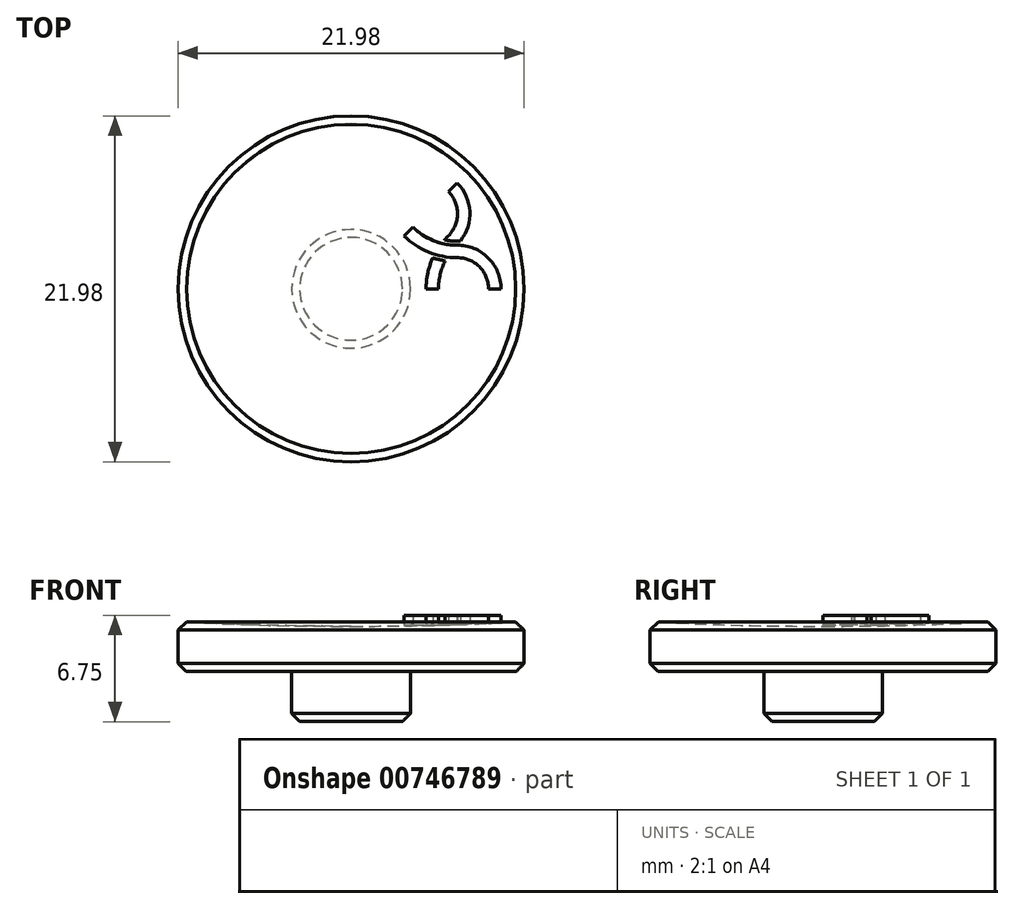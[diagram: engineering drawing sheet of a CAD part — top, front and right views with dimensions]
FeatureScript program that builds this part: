
annotation { "Feature Type Name" : "Feature", "Feature Type Description" : "" }
export const myFeature = defineFeature(function(context is Context, id is Id, definition is map)
    precondition{}
    {
        {
            var Q0;
            Q0=qCreatedBy(makeId("Top.planeOp"),FACE);
            var sketch = newSketch(context, id + "F0", { "sketchPlane" : qUnion([Q0])});
            skCircle(sketch, "E0", {"center": v(0, 0) * mm, "radius": 10.99 * mm});
            skCircle(sketch, "E1", {"center": v(0, 0) * mm, "radius": 3.77 * mm});
            skSolve(sketch);
        }
        {
            var Q0;
            Q0=makeQuery(id+"F0.imprint","IMPRINT",FACE,{"disambiguationData":[TD([[makeQuery(id+"F0.imprint","IMPRINT",EDGE,{"derivedFrom":sQuery(id+"F0.wireOp",EDGE,"E1")}),1.0]])]});
            var Q1;
            Q1=makeQuery(id+"F0.imprint","IMPRINT",FACE,{"disambiguationData":[TD([[makeQuery(id+"F0.imprint","IMPRINT",EDGE,{"derivedFrom":sQuery(id+"F0.wireOp",EDGE,"E0")}),1.0]])]});
            extrude(context, id + "F1", {"entities" : qUnion([Q0, Q1]), "depth" : 3.17 * mm, "offsetDistance" : 25.4 * mm});
        }
        {
            var Q0;
            Q0=makeQuery(id+"F0.imprint","IMPRINT",FACE,{"disambiguationData":[TD([[makeQuery(id+"F0.imprint","IMPRINT",EDGE,{"derivedFrom":sQuery(id+"F0.wireOp",EDGE,"E1")}),1.0]])]});
            extrude(context, id + "F2", {"entities" : qUnion([Q0]), "operationType" : NewBodyOperationType.ADD, "oppositeDirection" : true, "depth" : 3.17 * mm, "offsetDistance" : 25.4 * mm});
        }
        {
            var Q0;
            Q0=qCreatedBy(makeId("Front.planeOp"),FACE);
            var sketch = newSketch(context, id + "F3", { "sketchPlane" : qUnion([Q0])});
            skLineSegment(sketch, "E2", {"start": v(0, -33.46) * mm, "end": v(0, 35.26) * mm, "construction": true});
            skArc(sketch, "E3", {"start": v(0, 2.88) * mm, "mid": v(5.5, 2.95) * mm, "end": v(10.99, 3.18) * mm});
            skLineSegment(sketch, "E4", {"start": v(10.99, 3.18) * mm, "end": v(0, 3.17) * mm});
            skLineSegment(sketch, "E5", {"start": v(0, 3.18) * mm, "end": v(0, 2.88) * mm});
            skSolve(sketch);
        }
        {
            var Q0;
            Q0=makeQuery(id+"F3.imprint","IMPRINT",FACE,{"disambiguationData":[TD([[makeQuery(id+"F3.imprint","IMPRINT",EDGE,{"derivedFrom":sQuery(id+"F3.wireOp",EDGE,"E3")}),1.0]])]});
            var Q1;
            Q1=sQuery(id+"F3.wireOp",EDGE,"E2");
            revolve(context, id + "F4", {"operationType" : NewBodyOperationType.REMOVE, "surfaceOperationType" : NewSurfaceOperationType.NEW, "entities" : qUnion([Q0]), "axis" : qUnion([Q1]), "revolveType" : RevolveType.FULL, "oppositeDirection" : true});
        }
        {
            var Q0;
            Q0=qCreatedBy(makeId("Top.planeOp"),FACE);
            cPlane(context, id + "F5", {"entities" : qUnion([Q0]), "cplaneType" : CPlaneType.OFFSET, "offset" : 3.17 * mm, "width" : 152.4 * mm, "height" : 152.4 * mm});
        }
        {
            var Q0;
            Q0=qCreatedBy(id+"F5.planeOp",FACE);
            var sketch = newSketch(context, id + "F6", { "sketchPlane" : qUnion([Q0])});
            skLineSegment(sketch, "E6", {"start": v(0, 0) * mm, "end": v(10.99, 0) * mm});
            skLineSegment(sketch, "E7", {"start": v(0, 0) * mm, "end": v(7.77, 7.77) * mm});
            skLineSegment(sketch, "E8", {"start": v(0, 0) * mm, "end": v(0, 10.99) * mm});
            skCircle(sketch, "E9", {"center": v(0, 0) * mm, "radius": 4.76 * mm});
            skCircle(sketch, "E10", {"center": v(0, 0) * mm, "radius": 7.14 * mm});
            skCircle(sketch, "E11", {"center": v(0, 0) * mm, "radius": 9.53 * mm});
            skArc(sketch, "E12", {"start": v(9.53, 0) * mm, "mid": v(8.7, 1.97) * mm, "end": v(6.73, 2.78) * mm});
            skArc(sketch, "E13", {"start": v(3.37, 3.37) * mm, "mid": v(4.91, 2.34) * mm, "end": v(6.74, 1.98) * mm});
            skArc(sketch, "E14", {"start": v(8.73, 0) * mm, "mid": v(8.15, 1.4) * mm, "end": v(6.74, 1.98) * mm});
            skArc(sketch, "E15", {"start": v(3.93, 3.93) * mm, "mid": v(5.22, 3.07) * mm, "end": v(6.73, 2.78) * mm});
            skLineSegment(sketch, "E16", {"start": v(6.74, 1.98) * mm, "end": v(6.73, 2.78) * mm});
            skPoint(sketch, "E17", {"position": v(6.74, 2.38) * mm});
            skArc(sketch, "E18", {"start": v(6.72, 2.8) * mm, "mid": v(7.55, 4.77) * mm, "end": v(6.74, 6.74) * mm});
            skArc(sketch, "E19", {"start": v(6.17, 3.36) * mm, "mid": v(6.76, 4.77) * mm, "end": v(6.18, 6.18) * mm});
            skArc(sketch, "E20", {"start": v(6.17, 3.36) * mm, "mid": v(5.13, 1.82) * mm, "end": v(4.76, 0) * mm});
            skArc(sketch, "E21", {"start": v(6.72, 2.8) * mm, "mid": v(5.85, 1.52) * mm, "end": v(5.55, 0) * mm});
            skLineSegment(sketch, "E22", {"start": v(6.17, 3.36) * mm, "end": v(6.72, 2.8) * mm});
            skPoint(sketch, "E23", {"position": v(6.45, 3.08) * mm});
            skArc(sketch, "E24", {"start": v(5.2, 1.97) * mm, "mid": v(5.58, 1.86) * mm, "end": v(5.98, 1.78) * mm});
            skArc(sketch, "E25", {"start": v(5.93, 3.11) * mm, "mid": v(6.43, 3.04) * mm, "end": v(6.93, 3.04) * mm});
            skSolve(sketch);
        }
        {
            var Q0;
            {var subQ7=sQuery(id+"F6.wireOp",EDGE,"E12");Q0=makeQuery(id+"F6.imprint","IMPRINT",FACE,{"disambiguationData":[TD([[makeQuery(id+"F6.imprint","IMPRINT",EDGE,{"derivedFrom":subQ7}),1.0]])]});}
            var Q1;
            {var subQ0=sQuery(id+"F6.wireOp",EDGE,"E14");var subQ1=sQuery(id+"F6.wireOp",EDGE,"E10");var subQ2=makeQuery(id+"F6.imprint","INTERSECT",VERTEX,{"derivedFrom":[subQ1,subQ0]});Q1=makeQuery(id+"F6.imprint","IMPRINT",FACE,{"disambiguationData":[TD([[makeQuery(id+"F6.imprint","IMPRINT",EDGE,{"disambiguationData":[TD([[subQ2,-1.0]])],"derivedFrom":subQ1}),1.0]])]});}
            var Q2;
            {var subQ0=sQuery(id+"F6.wireOp",EDGE,"E16");var subQ1=sQuery(id+"F6.wireOp",EDGE,"E10");var subQ2=makeQuery(id+"F6.imprint","INTERSECT",VERTEX,{"derivedFrom":[subQ1,subQ0]});Q2=makeQuery(id+"F6.imprint","IMPRINT",FACE,{"disambiguationData":[TD([[makeQuery(id+"F6.imprint","IMPRINT",EDGE,{"disambiguationData":[TD([[subQ2,-1.0]])],"derivedFrom":subQ1}),-1.0]])]});}
            var Q3;
            {var subQ0=sQuery(id+"F6.wireOp",EDGE,"E21");var subQ1=sQuery(id+"F6.wireOp",EDGE,"E10");var subQ2=makeQuery(id+"F6.imprint","INTERSECT",VERTEX,{"derivedFrom":[subQ1,subQ0]});Q3=makeQuery(id+"F6.imprint","IMPRINT",FACE,{"disambiguationData":[TD([[makeQuery(id+"F6.imprint","IMPRINT",EDGE,{"disambiguationData":[TD([[subQ2,-1.0]])],"derivedFrom":subQ1}),-1.0]])]});}
            var Q4;
            {var subQ5=sQuery(id+"F6.wireOp",EDGE,"E10");var subQ7=sQuery(id+"F6.wireOp",EDGE,"E21");var subQ9=makeQuery(id+"F6.imprint","INTERSECT",VERTEX,{"derivedFrom":[subQ5,subQ7]});Q4=makeQuery(id+"F6.imprint","IMPRINT",FACE,{"disambiguationData":[TD([[makeQuery(id+"F6.imprint","IMPRINT",EDGE,{"disambiguationData":[TD([[subQ9,-1.0]])],"derivedFrom":subQ5}),1.0]])]});}
            var Q5;
            {var subQ0=sQuery(id+"F6.wireOp",EDGE,"E16");var subQ1=sQuery(id+"F6.wireOp",EDGE,"E10");var subQ2=makeQuery(id+"F6.imprint","INTERSECT",VERTEX,{"derivedFrom":[subQ1,subQ0]});Q5=makeQuery(id+"F6.imprint","IMPRINT",FACE,{"disambiguationData":[TD([[makeQuery(id+"F6.imprint","IMPRINT",EDGE,{"disambiguationData":[TD([[subQ2,-1.0]])],"derivedFrom":subQ1}),1.0]])]});}
            var Q6;
            {var subQ1=sQuery(id+"F6.wireOp",EDGE,"E7");var subQ3=sQuery(id+"F6.wireOp",EDGE,"E15");var subQ4=makeQuery(id+"F6.imprint","INTERSECT",VERTEX,{"derivedFrom":[subQ1,subQ3]});Q6=makeQuery(id+"F6.imprint","IMPRINT",FACE,{"disambiguationData":[TD([[makeQuery(id+"F6.imprint","IMPRINT",EDGE,{"disambiguationData":[TD([[subQ4,-1.0]])],"derivedFrom":subQ3}),-1.0]])]});}
            extrude(context, id + "F7", {"entities" : qUnion([Q0, Q1, Q2, Q3, Q4, Q5, Q6]), "operationType" : NewBodyOperationType.ADD, "depth" : 0.4 * mm, "offsetDistance" : 25.4 * mm, "hasSecondDirection" : true, "secondDirectionBound" : SecondDirectionBoundingType.UP_TO_NEXT, "secondDirectionOppositeDirection" : true, "secondDirectionDepth" : 25.4 * mm});
        }
        {
            var Q0;
            {var subQ5=sQuery(id+"F6.wireOp",EDGE,"E24");Q0=makeQuery(id+"F6.imprint","IMPRINT",FACE,{"disambiguationData":[TD([[makeQuery(id+"F6.imprint","IMPRINT",EDGE,{"derivedFrom":subQ5}),-1.0]])]});}
            var Q1;
            {var subQ0=sQuery(id+"F6.wireOp",EDGE,"E25");var subQ1=sQuery(id+"F6.wireOp",EDGE,"E10");var subQ2=makeQuery(id+"F6.imprint","INTERSECT",VERTEX,{"derivedFrom":[subQ1,subQ0]});Q1=makeQuery(id+"F6.imprint","IMPRINT",FACE,{"disambiguationData":[TD([[makeQuery(id+"F6.imprint","IMPRINT",EDGE,{"disambiguationData":[TD([[subQ2,-1.0]])],"derivedFrom":subQ1}),1.0]])]});}
            var Q2;
            {var subQ0=sQuery(id+"F6.wireOp",EDGE,"E25");var subQ1=sQuery(id+"F6.wireOp",EDGE,"E10");var subQ2=makeQuery(id+"F6.imprint","INTERSECT",VERTEX,{"derivedFrom":[subQ1,subQ0]});Q2=makeQuery(id+"F6.imprint","IMPRINT",FACE,{"disambiguationData":[TD([[makeQuery(id+"F6.imprint","IMPRINT",EDGE,{"disambiguationData":[TD([[subQ2,-1.0]])],"derivedFrom":subQ1}),-1.0]])]});}
            var Q3;
            {var subQ0=sQuery(id+"F6.wireOp",EDGE,"E22");var subQ1=sQuery(id+"F6.wireOp",EDGE,"E10");var subQ2=makeQuery(id+"F6.imprint","INTERSECT",VERTEX,{"derivedFrom":[subQ1,subQ0]});Q3=makeQuery(id+"F6.imprint","IMPRINT",FACE,{"disambiguationData":[TD([[makeQuery(id+"F6.imprint","IMPRINT",EDGE,{"disambiguationData":[TD([[subQ2,-1.0]])],"derivedFrom":subQ1}),1.0]])]});}
            var Q4;
            {var subQ7=sQuery(id+"F6.wireOp",EDGE,"E22");var subQ8=sQuery(id+"F6.wireOp",EDGE,"E10");var subQ9=makeQuery(id+"F6.imprint","INTERSECT",VERTEX,{"derivedFrom":[subQ8,subQ7]});Q4=makeQuery(id+"F6.imprint","IMPRINT",FACE,{"disambiguationData":[TD([[makeQuery(id+"F6.imprint","IMPRINT",EDGE,{"disambiguationData":[TD([[subQ9,-1.0]])],"derivedFrom":subQ8}),-1.0]])]});}
            extrude(context, id + "F8", {"entities" : qUnion([Q0, Q1, Q2, Q3, Q4]), "operationType" : NewBodyOperationType.ADD, "depth" : 0.4 * mm, "offsetDistance" : 25.4 * mm, "hasSecondDirection" : true, "secondDirectionBound" : SecondDirectionBoundingType.UP_TO_NEXT, "secondDirectionOppositeDirection" : true, "secondDirectionDepth" : 25.4 * mm});
        }
        {
            var Q0;
            Q0=makeQuery(id+"F2.opExtrude","CAP_EDGE",EDGE,{"disambiguationData":[OSD([sQuery(id+"F0.wireOp",EDGE,"E1")])],"isStart":false});
            var Q1;
            Q1=makeQuery(id+"F4.boolean.opBoolean","MERGE",EDGE,{"derivedFrom":[makeQuery(id+"F1.opExtrude","CAP_EDGE",EDGE,{"disambiguationData":[OSD([sQuery(id+"F0.wireOp",EDGE,"E0")])],"isStart":false}),makeQuery(id+"F4.opRevolve","SWEPT_EDGE",EDGE,{"disambiguationData":[OSD([sQuery(id+"F3.wireOp",EDGE,"E3"),sQuery(id+"F3.wireOp",EDGE,"E4")])]})]});
            var Q2;
            Q2=makeQuery(id+"F1.opExtrude","CAP_EDGE",EDGE,{"disambiguationData":[OSD([sQuery(id+"F0.wireOp",EDGE,"E0")])],"isStart":true});
            chamfer(context, id + "F9", {"entities" : qUnion([Q0, Q1, Q2]), "width" : 0.5 * mm, "tangentPropagation" : true});
        }
    });
